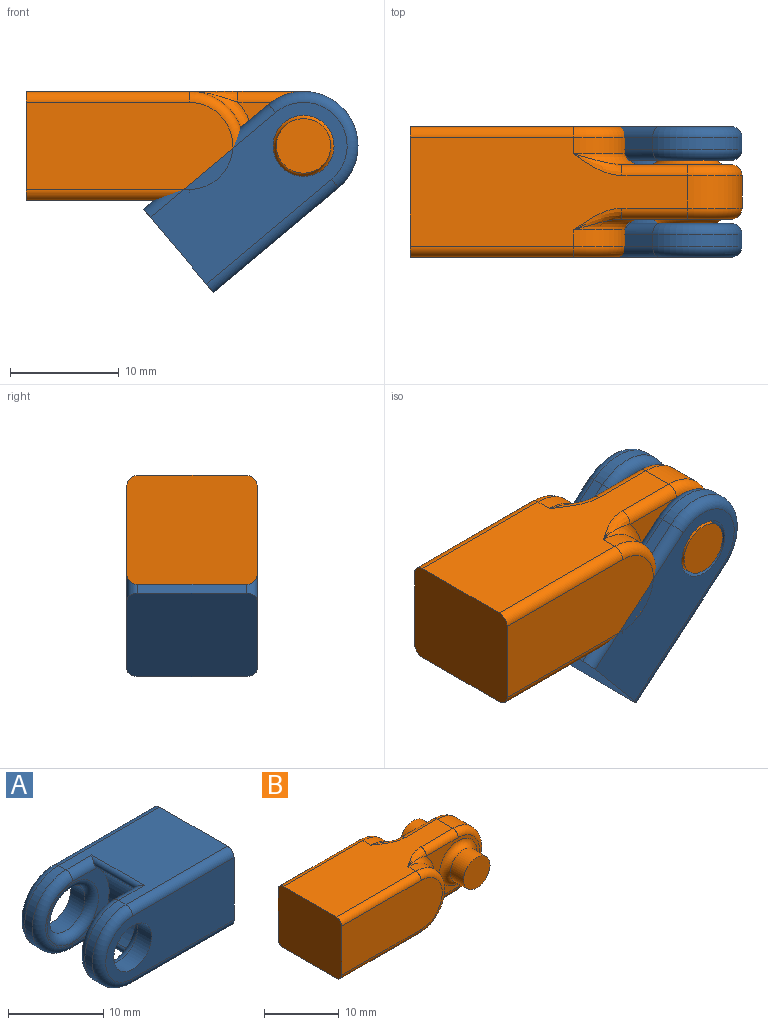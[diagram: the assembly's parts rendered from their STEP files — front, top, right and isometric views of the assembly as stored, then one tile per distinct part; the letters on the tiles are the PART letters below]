
ASSEMBLY  parts=2 mates=1
PART A: 28 faces, bbox 20.4x12x10.8 mm
  f0: plane 19x8mm, normal (0,-1,0), area 120.5mm2, adj f1,f12,f14,f15,f16
  f1: plane 12x10mm, normal (1,0,0), area 119.1mm2, adj f0,f2,f5,f6,f14,f16,f17,f19
  f2: plane 19x8mm, normal (0,1,0), area 120.5mm2, adj f1,f13,f17,f18,f19
  f3: plane 9.4x8mm, normal (0,-1,0), area 18.6mm2, adj f9,f23,f24,f25,f26
  f4: plane 9.4x8mm, normal (0,1,0), area 18.6mm2, adj f9,f20,f21,f22,f27
  f5: plane 15x10mm, normal (0,0,1), area 120.2mm2, adj f1,f7,f8,f10,f16,f19,f20,f25
  f6: plane 15x10mm, normal (0,0,-1), area 120.2mm2, adj f1,f7,f8,f11,f14,f17,f22,f23
  f7: cylinder r=5mm len=10mm, axis (0,1,0), area 17.3mm2, adj f5,f6,f18,f24
  f8: cylinder r=5mm len=10mm, axis (0,1,0), area 17.3mm2, adj f5,f6,f15,f21
  f9: cylinder r=5.4mm len=8.24mm, axis (0,-1,0), area 54.3mm2, adj f3,f4,f10,f11,f20,f22,f23,f25
  f10: cylinder r=0.5mm len=7.8mm, axis (0,-1,0), area 7.9mm2, adj f5,f9,f20,f25
  f11: cylinder r=0.5mm len=7.8mm, axis (0,-1,0), area 7.9mm2, adj f6,f9,f22,f23
  f12: cylinder r=2.8mm len=5.6mm, axis (0,1,0), area 36.9mm2, adj f0,f27
  f13: cylinder r=2.8mm len=5.6mm, axis (0,1,0), area 36.9mm2, adj f2,f26
  f14: cylinder r=1mm len=15mm, axis (1,0,0), area 23.6mm2, adj f0,f1,f6,f15
  f15: torus R=4mm, axis (0,1,0), area 22.9mm2, adj f0,f8,f14,f16
  f16: cylinder r=1mm len=15mm, axis (-1,0,0), area 23.6mm2, adj f0,f1,f5,f15
  f17: cylinder r=1mm len=15mm, axis (-1,0,0), area 23.6mm2, adj f1,f2,f6,f18
  f18: torus R=4mm, axis (0,1,0), area 22.9mm2, adj f2,f7,f17,f19
  f19: cylinder r=1mm len=15mm, axis (1,0,0), area 23.6mm2, adj f1,f2,f5,f18
  f20: cylinder r=1mm len=3.82mm, axis (1,0,0), area 5.5mm2, adj f4,f5,f9,f10,f21
  f21: torus R=4mm, axis (0,1,0), area 22.9mm2, adj f4,f8,f20,f22
  f22: cylinder r=1mm len=3.82mm, axis (-1,0,0), area 5.5mm2, adj f4,f6,f9,f11,f21
  f23: cylinder r=1mm len=3.82mm, axis (-1,0,0), area 5.5mm2, adj f3,f6,f9,f11,f24
  f24: torus R=4mm, axis (0,1,0), area 22.9mm2, adj f3,f7,f23,f25
  f25: cylinder r=1mm len=3.82mm, axis (-1,0,0), area 5.5mm2, adj f3,f5,f9,f10,f24
  f26: torus R=3.8mm, axis (0,1,0), area 31.2mm2, adj f3,f13
  f27: torus R=3.8mm, axis (0,1,0), area 31.2mm2, adj f4,f12
PART B: 34 faces, bbox 30.9x12x14.5 mm
  f0: plane 10.03x8mm, normal (0,1,0), area 26.5mm2, adj f26,f28,f29,f30,f32
  f1: plane 19x8mm, normal (0,1,0), area 145.1mm2, adj f2,f23,f24,f25
  f2: plane 12x10mm, normal (-1,0,0), area 119.1mm2, adj f1,f3,f5,f6,f20,f22,f23,f25
  f3: plane 19x8mm, normal (0,-1,0), area 145.1mm2, adj f2,f20,f21,f22
  f4: plane 10.03x8mm, normal (0,-1,0), area 26.5mm2, adj f14,f16,f17,f18,f33
  f5: plane 25.5x10mm, normal (0,0,1), area 188mm2, adj f2,f7,f8,f9,f18,f19,f22,f25
  f6: plane 25.5x10mm, normal (0,0,-1), area 188mm2, adj f2,f7,f8,f9,f14,f15,f20,f23
  f7: cylinder r=5mm len=10mm, axis (0,-1,0), area 23.6mm2, adj f5,f6,f17,f21
  f8: cylinder r=5mm len=10mm, axis (0,-1,0), area 23.6mm2, adj f5,f6,f24,f29
  f9: cylinder r=5mm len=10mm, axis (0,-1,0), area 47.1mm2, adj f5,f6,f16,f28
  f10: plane 5x5mm, normal (0,-1,0), area 19.6mm2, adj f11
  f11: cylinder r=2.5mm len=5mm, axis (0,1,0), area 39.3mm2, adj f10,f33
  f12: cylinder r=2.5mm len=5mm, axis (0,1,0), area 39.3mm2, adj f13,f32
  f13: plane 5x5mm, normal (0,1,0), area 19.6mm2, adj f12
  f14: cylinder r=1mm len=6.03mm, axis (1,0,0), area 9.5mm2, adj f4,f6,f15,f16
  f15: bspline ~5.15x2mm, area 3.8mm2, adj f6,f14,f17
  f16: torus R=4mm, axis (0,1,0), area 22.9mm2, adj f4,f9,f14,f18
  f17: torus R=6mm, axis (0,1,0), area 18.2mm2, adj f4,f7,f15,f19
  f18: cylinder r=1mm len=6.03mm, axis (-1,0,0), area 9.5mm2, adj f4,f5,f16,f19
  f19: bspline ~4.47x2mm, area 3.8mm2, adj f5,f17,f18
  f20: cylinder r=1mm len=15mm, axis (1,0,0), area 23.6mm2, adj f2,f3,f6,f21
  f21: torus R=4mm, axis (0,1,0), area 22.9mm2, adj f3,f7,f20,f22
  f22: cylinder r=1mm len=15mm, axis (-1,0,0), area 23.6mm2, adj f2,f3,f5,f21
  f23: cylinder r=1mm len=15mm, axis (-1,0,0), area 23.6mm2, adj f1,f2,f6,f24
  f24: torus R=4mm, axis (0,1,0), area 22.9mm2, adj f1,f8,f23,f25
  f25: cylinder r=1mm len=15mm, axis (1,0,0), area 23.6mm2, adj f1,f2,f5,f24
  f26: cylinder r=1mm len=6.03mm, axis (-1,0,0), area 9.5mm2, adj f0,f6,f27,f28
  f27: bspline ~5.15x2mm, area 3.8mm2, adj f6,f26,f29
  f28: torus R=4mm, axis (0,1,0), area 22.9mm2, adj f0,f9,f26,f30
  f29: torus R=6mm, axis (0,1,0), area 18.2mm2, adj f0,f8,f27,f31
  f30: cylinder r=1mm len=6.03mm, axis (1,0,0), area 9.5mm2, adj f0,f5,f28,f31
  f31: bspline ~5.15x2mm, area 3.8mm2, adj f5,f29,f30
  f32: torus R=3.5mm, axis (0,1,0), area 28.3mm2, adj f0,f12
  f33: torus R=3.5mm, axis (0,1,0), area 28.3mm2, adj f4,f11
PLACE A rot(axis=(0,1,0),140deg) t=(-7.9,6.32,1.37)mm
PLACE B t=(14.8,6.32,-0.38)mm fixed
MATE revolute B.f11 <-> A.f8  axis (0,-1,0) through (3.77,10.39,4.62)mm
